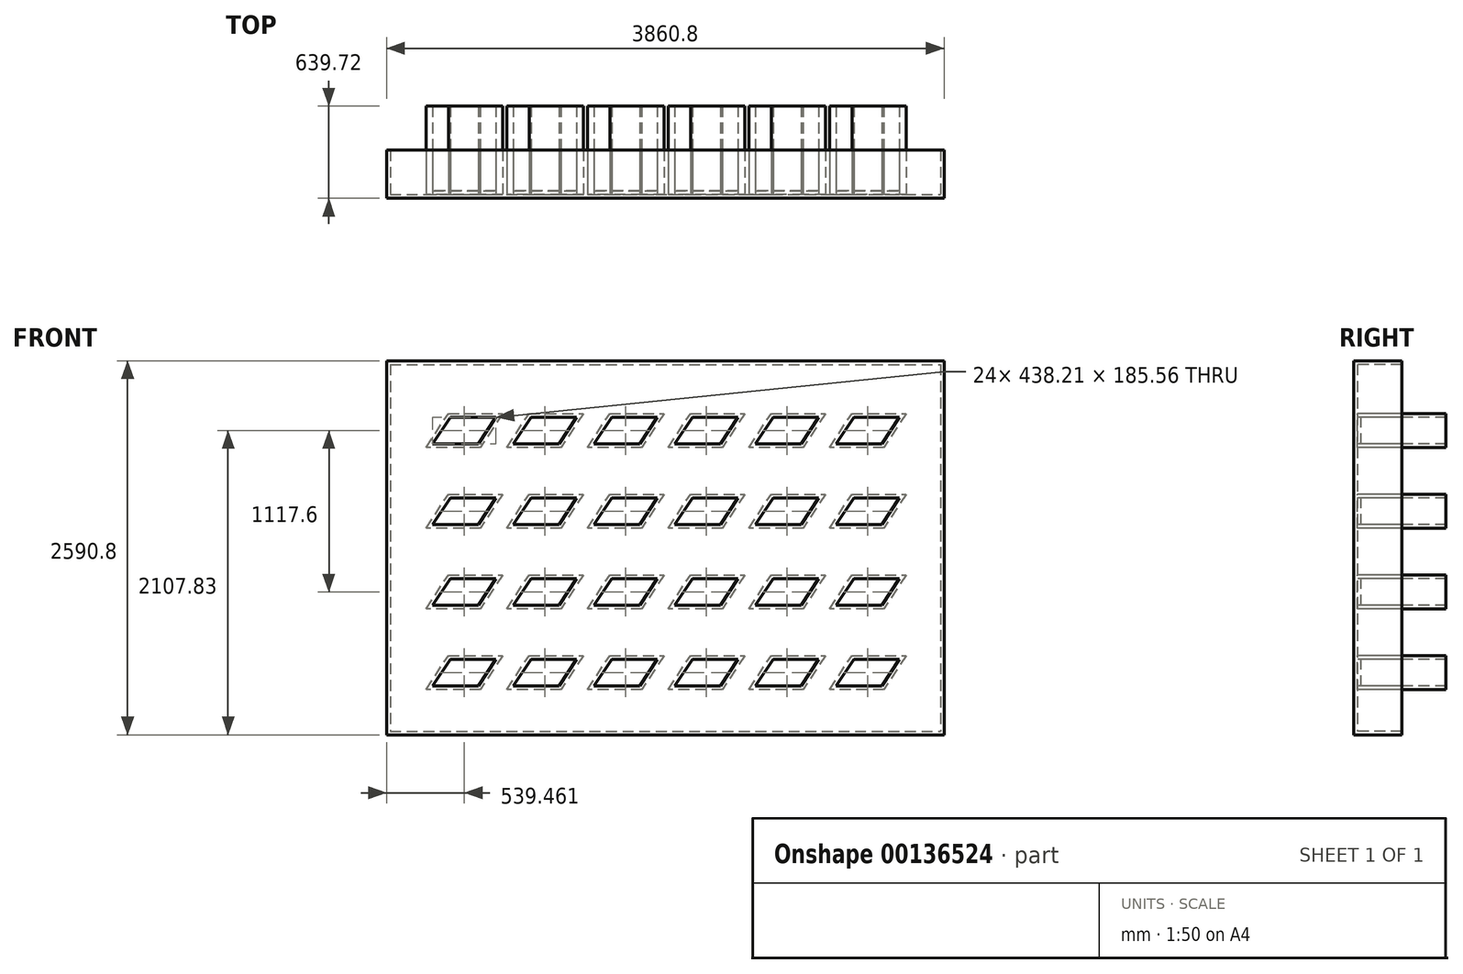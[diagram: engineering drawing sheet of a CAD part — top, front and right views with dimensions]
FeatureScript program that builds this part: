
annotation { "Feature Type Name" : "Feature", "Feature Type Description" : "" }
export const myFeature = defineFeature(function(context is Context, id is Id, definition is map)
    precondition{}
    {
        {
            var Q0;
            Q0=qCreatedBy(makeId("Front.planeOp"),FACE);
            var sketch = newSketch(context, id + "F0", { "sketchPlane" : qUnion([Q0])});
            skLineSegment(sketch, "E0.bottom", {"start": v(-2595.67, 2540) * mm, "end": v(1214.33, 2540) * mm});
            skLineSegment(sketch, "E0.top", {"start": v(-2595.67, 0) * mm, "end": v(1214.33, 0) * mm});
            skLineSegment(sketch, "E0.left", {"start": v(-2595.67, 2540) * mm, "end": v(-2595.67, 0) * mm});
            skLineSegment(sketch, "E0.right", {"start": v(1214.33, 2540) * mm, "end": v(1214.33, 0) * mm});
            skLineSegment(sketch, "E1", {"start": v(-2192.33, 2200.61) * mm, "end": v(-1815.39, 2200.61) * mm});
            skLineSegment(sketch, "E2", {"start": v(-1815.39, 2200.61) * mm, "end": v(-1970.89, 1964.26) * mm});
            skLineSegment(sketch, "E3", {"start": v(-1970.89, 1964.26) * mm, "end": v(-2347.83, 1964.26) * mm});
            skLineSegment(sketch, "E4", {"start": v(-2347.83, 1964.26) * mm, "end": v(-2192.33, 2200.61) * mm});
            skLineSegment(sketch, "E5.0.1.0", {"start": v(-2192.33, 1641.81) * mm, "end": v(-1815.39, 1641.81) * mm});
            skLineSegment(sketch, "E5.0.1.1", {"start": v(-2347.83, 1405.46) * mm, "end": v(-2192.33, 1641.81) * mm});
            skLineSegment(sketch, "E5.0.1.2", {"start": v(-1970.89, 1405.46) * mm, "end": v(-2347.83, 1405.46) * mm});
            skLineSegment(sketch, "E5.0.1.3", {"start": v(-1815.39, 1641.81) * mm, "end": v(-1970.89, 1405.46) * mm});
            skLineSegment(sketch, "E5.1.0.0", {"start": v(-1633.53, 2200.61) * mm, "end": v(-1256.59, 2200.61) * mm});
            skLineSegment(sketch, "E5.1.0.1", {"start": v(-1789.03, 1964.26) * mm, "end": v(-1633.53, 2200.61) * mm});
            skLineSegment(sketch, "E5.1.0.2", {"start": v(-1412.09, 1964.26) * mm, "end": v(-1789.03, 1964.26) * mm});
            skLineSegment(sketch, "E5.1.0.3", {"start": v(-1256.59, 2200.61) * mm, "end": v(-1412.09, 1964.26) * mm});
            skLineSegment(sketch, "E5.1.1.0", {"start": v(-1633.53, 1641.81) * mm, "end": v(-1256.59, 1641.81) * mm});
            skLineSegment(sketch, "E5.1.1.1", {"start": v(-1789.03, 1405.46) * mm, "end": v(-1633.53, 1641.81) * mm});
            skLineSegment(sketch, "E5.1.1.2", {"start": v(-1412.09, 1405.46) * mm, "end": v(-1789.03, 1405.46) * mm});
            skLineSegment(sketch, "E5.1.1.3", {"start": v(-1256.59, 1641.81) * mm, "end": v(-1412.09, 1405.46) * mm});
            skLineSegment(sketch, "E5.2.0.0", {"start": v(-1074.73, 2200.61) * mm, "end": v(-697.79, 2200.61) * mm});
            skLineSegment(sketch, "E5.2.0.1", {"start": v(-1230.23, 1964.26) * mm, "end": v(-1074.73, 2200.61) * mm});
            skLineSegment(sketch, "E5.2.0.2", {"start": v(-853.29, 1964.26) * mm, "end": v(-1230.23, 1964.26) * mm});
            skLineSegment(sketch, "E5.2.0.3", {"start": v(-697.79, 2200.61) * mm, "end": v(-853.29, 1964.26) * mm});
            skLineSegment(sketch, "E5.2.1.0", {"start": v(-1074.73, 1641.81) * mm, "end": v(-697.79, 1641.81) * mm});
            skLineSegment(sketch, "E5.2.1.1", {"start": v(-1230.23, 1405.46) * mm, "end": v(-1074.73, 1641.81) * mm});
            skLineSegment(sketch, "E5.2.1.2", {"start": v(-853.29, 1405.46) * mm, "end": v(-1230.23, 1405.46) * mm});
            skLineSegment(sketch, "E5.2.1.3", {"start": v(-697.79, 1641.81) * mm, "end": v(-853.29, 1405.46) * mm});
            skLineSegment(sketch, "E5.direction1", {"start": v(-2192.33, 2200.61) * mm, "end": v(-1633.53, 2200.61) * mm, "construction": true});
            skLineSegment(sketch, "E5.direction2", {"start": v(-2192.33, 2200.61) * mm, "end": v(-2192.33, 1641.81) * mm, "construction": true});
            skLineSegment(sketch, "E6.0.0.2", {"start": v(-2192.33, 1083.01) * mm, "end": v(-1815.39, 1083.01) * mm});
            skLineSegment(sketch, "E6.3.0.2", {"start": v(-2347.83, 846.66) * mm, "end": v(-2192.33, 1083.01) * mm});
            skLineSegment(sketch, "E6.6.0.2", {"start": v(-1970.89, 846.66) * mm, "end": v(-2347.83, 846.66) * mm});
            skLineSegment(sketch, "E6.9.0.2", {"start": v(-1815.39, 1083.01) * mm, "end": v(-1970.89, 846.66) * mm});
            skLineSegment(sketch, "E6.0.0.3", {"start": v(-2192.33, 524.21) * mm, "end": v(-1815.39, 524.21) * mm});
            skLineSegment(sketch, "E6.3.0.3", {"start": v(-2347.83, 287.86) * mm, "end": v(-2192.33, 524.21) * mm});
            skLineSegment(sketch, "E6.6.0.3", {"start": v(-1970.89, 287.86) * mm, "end": v(-2347.83, 287.86) * mm});
            skLineSegment(sketch, "E6.9.0.3", {"start": v(-1815.39, 524.21) * mm, "end": v(-1970.89, 287.86) * mm});
            skLineSegment(sketch, "E6.0.1.2", {"start": v(-1633.53, 1083.01) * mm, "end": v(-1256.59, 1083.01) * mm});
            skLineSegment(sketch, "E6.3.1.2", {"start": v(-1789.03, 846.66) * mm, "end": v(-1633.53, 1083.01) * mm});
            skLineSegment(sketch, "E6.6.1.2", {"start": v(-1412.09, 846.66) * mm, "end": v(-1789.03, 846.66) * mm});
            skLineSegment(sketch, "E6.9.1.2", {"start": v(-1256.59, 1083.01) * mm, "end": v(-1412.09, 846.66) * mm});
            skLineSegment(sketch, "E6.0.1.3", {"start": v(-1633.53, 524.21) * mm, "end": v(-1256.59, 524.21) * mm});
            skLineSegment(sketch, "E6.3.1.3", {"start": v(-1789.03, 287.86) * mm, "end": v(-1633.53, 524.21) * mm});
            skLineSegment(sketch, "E6.6.1.3", {"start": v(-1412.09, 287.86) * mm, "end": v(-1789.03, 287.86) * mm});
            skLineSegment(sketch, "E6.9.1.3", {"start": v(-1256.59, 524.21) * mm, "end": v(-1412.09, 287.86) * mm});
            skLineSegment(sketch, "E6.0.2.2", {"start": v(-1074.73, 1083.01) * mm, "end": v(-697.79, 1083.01) * mm});
            skLineSegment(sketch, "E6.3.2.2", {"start": v(-1230.23, 846.66) * mm, "end": v(-1074.73, 1083.01) * mm});
            skLineSegment(sketch, "E6.6.2.2", {"start": v(-853.29, 846.66) * mm, "end": v(-1230.23, 846.66) * mm});
            skLineSegment(sketch, "E6.9.2.2", {"start": v(-697.79, 1083.01) * mm, "end": v(-853.29, 846.66) * mm});
            skLineSegment(sketch, "E6.0.2.3", {"start": v(-1074.73, 524.21) * mm, "end": v(-697.79, 524.21) * mm});
            skLineSegment(sketch, "E6.3.2.3", {"start": v(-1230.23, 287.86) * mm, "end": v(-1074.73, 524.21) * mm});
            skLineSegment(sketch, "E6.6.2.3", {"start": v(-853.29, 287.86) * mm, "end": v(-1230.23, 287.86) * mm});
            skLineSegment(sketch, "E6.9.2.3", {"start": v(-697.79, 524.21) * mm, "end": v(-853.29, 287.86) * mm});
            skLineSegment(sketch, "E7.0.3.0", {"start": v(-515.93, 2200.61) * mm, "end": v(-138.99, 2200.61) * mm});
            skLineSegment(sketch, "E7.3.3.0", {"start": v(-671.43, 1964.26) * mm, "end": v(-515.93, 2200.61) * mm});
            skLineSegment(sketch, "E7.6.3.0", {"start": v(-294.49, 1964.26) * mm, "end": v(-671.43, 1964.26) * mm});
            skLineSegment(sketch, "E7.9.3.0", {"start": v(-138.99, 2200.61) * mm, "end": v(-294.49, 1964.26) * mm});
            skLineSegment(sketch, "E7.0.3.1", {"start": v(-515.93, 1641.81) * mm, "end": v(-138.99, 1641.81) * mm});
            skLineSegment(sketch, "E7.3.3.1", {"start": v(-671.43, 1405.46) * mm, "end": v(-515.93, 1641.81) * mm});
            skLineSegment(sketch, "E7.6.3.1", {"start": v(-294.49, 1405.46) * mm, "end": v(-671.43, 1405.46) * mm});
            skLineSegment(sketch, "E7.9.3.1", {"start": v(-138.99, 1641.81) * mm, "end": v(-294.49, 1405.46) * mm});
            skLineSegment(sketch, "E7.0.3.2", {"start": v(-515.93, 1083.01) * mm, "end": v(-138.99, 1083.01) * mm});
            skLineSegment(sketch, "E7.3.3.2", {"start": v(-671.43, 846.66) * mm, "end": v(-515.93, 1083.01) * mm});
            skLineSegment(sketch, "E7.6.3.2", {"start": v(-294.49, 846.66) * mm, "end": v(-671.43, 846.66) * mm});
            skLineSegment(sketch, "E7.9.3.2", {"start": v(-138.99, 1083.01) * mm, "end": v(-294.49, 846.66) * mm});
            skLineSegment(sketch, "E7.0.3.3", {"start": v(-515.93, 524.21) * mm, "end": v(-138.99, 524.21) * mm});
            skLineSegment(sketch, "E7.3.3.3", {"start": v(-671.43, 287.86) * mm, "end": v(-515.93, 524.21) * mm});
            skLineSegment(sketch, "E7.6.3.3", {"start": v(-294.49, 287.86) * mm, "end": v(-671.43, 287.86) * mm});
            skLineSegment(sketch, "E7.9.3.3", {"start": v(-138.99, 524.21) * mm, "end": v(-294.49, 287.86) * mm});
            skLineSegment(sketch, "E7.0.4.0", {"start": v(42.87, 2200.61) * mm, "end": v(419.81, 2200.61) * mm});
            skLineSegment(sketch, "E7.3.4.0", {"start": v(-112.63, 1964.26) * mm, "end": v(42.87, 2200.61) * mm});
            skLineSegment(sketch, "E7.6.4.0", {"start": v(264.31, 1964.26) * mm, "end": v(-112.63, 1964.26) * mm});
            skLineSegment(sketch, "E7.9.4.0", {"start": v(419.81, 2200.61) * mm, "end": v(264.31, 1964.26) * mm});
            skLineSegment(sketch, "E7.0.4.1", {"start": v(42.87, 1641.81) * mm, "end": v(419.81, 1641.81) * mm});
            skLineSegment(sketch, "E7.3.4.1", {"start": v(-112.63, 1405.46) * mm, "end": v(42.87, 1641.81) * mm});
            skLineSegment(sketch, "E7.6.4.1", {"start": v(264.31, 1405.46) * mm, "end": v(-112.63, 1405.46) * mm});
            skLineSegment(sketch, "E7.9.4.1", {"start": v(419.81, 1641.81) * mm, "end": v(264.31, 1405.46) * mm});
            skLineSegment(sketch, "E7.0.4.2", {"start": v(42.87, 1083.01) * mm, "end": v(419.81, 1083.01) * mm});
            skLineSegment(sketch, "E7.3.4.2", {"start": v(-112.63, 846.66) * mm, "end": v(42.87, 1083.01) * mm});
            skLineSegment(sketch, "E7.6.4.2", {"start": v(264.31, 846.66) * mm, "end": v(-112.63, 846.66) * mm});
            skLineSegment(sketch, "E7.9.4.2", {"start": v(419.81, 1083.01) * mm, "end": v(264.31, 846.66) * mm});
            skLineSegment(sketch, "E7.0.4.3", {"start": v(42.87, 524.21) * mm, "end": v(419.81, 524.21) * mm});
            skLineSegment(sketch, "E7.3.4.3", {"start": v(-112.63, 287.86) * mm, "end": v(42.87, 524.21) * mm});
            skLineSegment(sketch, "E7.6.4.3", {"start": v(264.31, 287.86) * mm, "end": v(-112.63, 287.86) * mm});
            skLineSegment(sketch, "E7.9.4.3", {"start": v(419.81, 524.21) * mm, "end": v(264.31, 287.86) * mm});
            skLineSegment(sketch, "E7.0.5.0", {"start": v(601.67, 2200.61) * mm, "end": v(978.61, 2200.61) * mm});
            skLineSegment(sketch, "E7.3.5.0", {"start": v(446.17, 1964.26) * mm, "end": v(601.67, 2200.61) * mm});
            skLineSegment(sketch, "E7.6.5.0", {"start": v(823.11, 1964.26) * mm, "end": v(446.17, 1964.26) * mm});
            skLineSegment(sketch, "E7.9.5.0", {"start": v(978.61, 2200.61) * mm, "end": v(823.11, 1964.26) * mm});
            skLineSegment(sketch, "E7.0.5.1", {"start": v(601.67, 1641.81) * mm, "end": v(978.61, 1641.81) * mm});
            skLineSegment(sketch, "E7.3.5.1", {"start": v(446.17, 1405.46) * mm, "end": v(601.67, 1641.81) * mm});
            skLineSegment(sketch, "E7.6.5.1", {"start": v(823.11, 1405.46) * mm, "end": v(446.17, 1405.46) * mm});
            skLineSegment(sketch, "E7.9.5.1", {"start": v(978.61, 1641.81) * mm, "end": v(823.11, 1405.46) * mm});
            skLineSegment(sketch, "E7.0.5.2", {"start": v(601.67, 1083.01) * mm, "end": v(978.61, 1083.01) * mm});
            skLineSegment(sketch, "E7.3.5.2", {"start": v(446.17, 846.66) * mm, "end": v(601.67, 1083.01) * mm});
            skLineSegment(sketch, "E7.6.5.2", {"start": v(823.11, 846.66) * mm, "end": v(446.17, 846.66) * mm});
            skLineSegment(sketch, "E7.9.5.2", {"start": v(978.61, 1083.01) * mm, "end": v(823.11, 846.66) * mm});
            skLineSegment(sketch, "E7.0.5.3", {"start": v(601.67, 524.21) * mm, "end": v(978.61, 524.21) * mm});
            skLineSegment(sketch, "E7.3.5.3", {"start": v(446.17, 287.86) * mm, "end": v(601.67, 524.21) * mm});
            skLineSegment(sketch, "E7.6.5.3", {"start": v(823.11, 287.86) * mm, "end": v(446.17, 287.86) * mm});
            skLineSegment(sketch, "E7.9.5.3", {"start": v(978.61, 524.21) * mm, "end": v(823.11, 287.86) * mm});
            skSolve(sketch);
        }
        {
            var Q0;
            Q0=makeQuery(id+"F0.imprint","IMPRINT",FACE,{"disambiguationData":[TD([[makeQuery(id+"F0.imprint","IMPRINT",EDGE,{"derivedFrom":sQuery(id+"F0.wireOp",EDGE,"E7.0.5.2")}),-1.0]])]});
            var Q1;
            Q1=makeQuery(id+"F0.imprint","IMPRINT",FACE,{"disambiguationData":[TD([[makeQuery(id+"F0.imprint","IMPRINT",EDGE,{"derivedFrom":sQuery(id+"F0.wireOp",EDGE,"E7.0.5.3")}),-1.0]])]});
            var Q2;
            Q2=makeQuery(id+"F0.imprint","IMPRINT",FACE,{"disambiguationData":[TD([[makeQuery(id+"F0.imprint","IMPRINT",EDGE,{"derivedFrom":sQuery(id+"F0.wireOp",EDGE,"E7.0.5.1")}),-1.0]])]});
            var Q3;
            Q3=makeQuery(id+"F0.imprint","IMPRINT",FACE,{"disambiguationData":[TD([[makeQuery(id+"F0.imprint","IMPRINT",EDGE,{"derivedFrom":sQuery(id+"F0.wireOp",EDGE,"E7.0.5.0")}),-1.0]])]});
            var Q4;
            Q4=makeQuery(id+"F0.imprint","IMPRINT",FACE,{"disambiguationData":[TD([[makeQuery(id+"F0.imprint","IMPRINT",EDGE,{"derivedFrom":sQuery(id+"F0.wireOp",EDGE,"E7.0.4.3")}),-1.0]])]});
            var Q5;
            Q5=makeQuery(id+"F0.imprint","IMPRINT",FACE,{"disambiguationData":[TD([[makeQuery(id+"F0.imprint","IMPRINT",EDGE,{"derivedFrom":sQuery(id+"F0.wireOp",EDGE,"E7.0.4.2")}),-1.0]])]});
            var Q6;
            Q6=makeQuery(id+"F0.imprint","IMPRINT",FACE,{"disambiguationData":[TD([[makeQuery(id+"F0.imprint","IMPRINT",EDGE,{"derivedFrom":sQuery(id+"F0.wireOp",EDGE,"E7.0.4.1")}),-1.0]])]});
            var Q7;
            Q7=makeQuery(id+"F0.imprint","IMPRINT",FACE,{"disambiguationData":[TD([[makeQuery(id+"F0.imprint","IMPRINT",EDGE,{"derivedFrom":sQuery(id+"F0.wireOp",EDGE,"E7.0.4.0")}),-1.0]])]});
            var Q8;
            Q8=makeQuery(id+"F0.imprint","IMPRINT",FACE,{"disambiguationData":[TD([[makeQuery(id+"F0.imprint","IMPRINT",EDGE,{"derivedFrom":sQuery(id+"F0.wireOp",EDGE,"E7.0.3.3")}),-1.0]])]});
            var Q9;
            Q9=makeQuery(id+"F0.imprint","IMPRINT",FACE,{"disambiguationData":[TD([[makeQuery(id+"F0.imprint","IMPRINT",EDGE,{"derivedFrom":sQuery(id+"F0.wireOp",EDGE,"E7.0.3.2")}),-1.0]])]});
            var Q10;
            Q10=makeQuery(id+"F0.imprint","IMPRINT",FACE,{"disambiguationData":[TD([[makeQuery(id+"F0.imprint","IMPRINT",EDGE,{"derivedFrom":sQuery(id+"F0.wireOp",EDGE,"E7.0.3.1")}),-1.0]])]});
            var Q11;
            Q11=makeQuery(id+"F0.imprint","IMPRINT",FACE,{"disambiguationData":[TD([[makeQuery(id+"F0.imprint","IMPRINT",EDGE,{"derivedFrom":sQuery(id+"F0.wireOp",EDGE,"E7.0.3.0")}),-1.0]])]});
            var Q12;
            Q12=makeQuery(id+"F0.imprint","IMPRINT",FACE,{"disambiguationData":[TD([[makeQuery(id+"F0.imprint","IMPRINT",EDGE,{"derivedFrom":sQuery(id+"F0.wireOp",EDGE,"E6.0.2.3")}),-1.0]])]});
            var Q13;
            Q13=makeQuery(id+"F0.imprint","IMPRINT",FACE,{"disambiguationData":[TD([[makeQuery(id+"F0.imprint","IMPRINT",EDGE,{"derivedFrom":sQuery(id+"F0.wireOp",EDGE,"E6.0.2.2")}),-1.0]])]});
            var Q14;
            Q14=makeQuery(id+"F0.imprint","IMPRINT",FACE,{"disambiguationData":[TD([[makeQuery(id+"F0.imprint","IMPRINT",EDGE,{"derivedFrom":sQuery(id+"F0.wireOp",EDGE,"E5.2.1.0")}),-1.0]])]});
            var Q15;
            Q15=makeQuery(id+"F0.imprint","IMPRINT",FACE,{"disambiguationData":[TD([[makeQuery(id+"F0.imprint","IMPRINT",EDGE,{"derivedFrom":sQuery(id+"F0.wireOp",EDGE,"E5.2.0.0")}),-1.0]])]});
            var Q16;
            Q16=makeQuery(id+"F0.imprint","IMPRINT",FACE,{"disambiguationData":[TD([[makeQuery(id+"F0.imprint","IMPRINT",EDGE,{"derivedFrom":sQuery(id+"F0.wireOp",EDGE,"E6.0.1.3")}),-1.0]])]});
            var Q17;
            Q17=makeQuery(id+"F0.imprint","IMPRINT",FACE,{"disambiguationData":[TD([[makeQuery(id+"F0.imprint","IMPRINT",EDGE,{"derivedFrom":sQuery(id+"F0.wireOp",EDGE,"E6.0.1.2")}),-1.0]])]});
            var Q18;
            Q18=makeQuery(id+"F0.imprint","IMPRINT",FACE,{"disambiguationData":[TD([[makeQuery(id+"F0.imprint","IMPRINT",EDGE,{"derivedFrom":sQuery(id+"F0.wireOp",EDGE,"E5.1.1.0")}),-1.0]])]});
            var Q19;
            Q19=makeQuery(id+"F0.imprint","IMPRINT",FACE,{"disambiguationData":[TD([[makeQuery(id+"F0.imprint","IMPRINT",EDGE,{"derivedFrom":sQuery(id+"F0.wireOp",EDGE,"E5.1.0.0")}),-1.0]])]});
            var Q20;
            Q20=makeQuery(id+"F0.imprint","IMPRINT",FACE,{"disambiguationData":[TD([[makeQuery(id+"F0.imprint","IMPRINT",EDGE,{"derivedFrom":sQuery(id+"F0.wireOp",EDGE,"E6.0.0.3")}),-1.0]])]});
            var Q21;
            Q21=makeQuery(id+"F0.imprint","IMPRINT",FACE,{"disambiguationData":[TD([[makeQuery(id+"F0.imprint","IMPRINT",EDGE,{"derivedFrom":sQuery(id+"F0.wireOp",EDGE,"E6.0.0.2")}),-1.0]])]});
            var Q22;
            Q22=makeQuery(id+"F0.imprint","IMPRINT",FACE,{"disambiguationData":[TD([[makeQuery(id+"F0.imprint","IMPRINT",EDGE,{"derivedFrom":sQuery(id+"F0.wireOp",EDGE,"E5.0.1.0")}),-1.0]])]});
            var Q23;
            Q23=makeQuery(id+"F0.imprint","IMPRINT",FACE,{"disambiguationData":[TD([[makeQuery(id+"F0.imprint","IMPRINT",EDGE,{"derivedFrom":sQuery(id+"F0.wireOp",EDGE,"E1")}),-1.0]])]});
            extrude(context, id + "F1", {"entities" : qUnion([Q0, Q1, Q2, Q3, Q4, Q5, Q6, Q7, Q8, Q9, Q10, Q11, Q12, Q13, Q14, Q15, Q16, Q17, Q18, Q19, Q20, Q21, Q22, Q23]), "oppositeDirection" : true, "depth" : 614.32 * mm});
        }
        {
            var Q0;
            Q0=makeQuery(id+"F1.opExtrude","CAP_FACE",FACE,{"disambiguationData":[OSD([sQuery(id+"F0.wireOp",EDGE,"E7.0.5.0"),sQuery(id+"F0.wireOp",EDGE,"E7.3.5.0"),sQuery(id+"F0.wireOp",EDGE,"E7.6.5.0"),sQuery(id+"F0.wireOp",EDGE,"E7.9.5.0")])],"isStart":false});
            var Q1;
            Q1=makeQuery(id+"F1.opExtrude","CAP_FACE",FACE,{"disambiguationData":[OSD([sQuery(id+"F0.wireOp",EDGE,"E7.0.5.1"),sQuery(id+"F0.wireOp",EDGE,"E7.3.5.1"),sQuery(id+"F0.wireOp",EDGE,"E7.6.5.1"),sQuery(id+"F0.wireOp",EDGE,"E7.9.5.1")])],"isStart":false});
            var Q2;
            Q2=makeQuery(id+"F1.opExtrude","CAP_FACE",FACE,{"disambiguationData":[OSD([sQuery(id+"F0.wireOp",EDGE,"E7.0.4.1"),sQuery(id+"F0.wireOp",EDGE,"E7.3.4.1"),sQuery(id+"F0.wireOp",EDGE,"E7.6.4.1"),sQuery(id+"F0.wireOp",EDGE,"E7.9.4.1")])],"isStart":false});
            var Q3;
            Q3=makeQuery(id+"F1.opExtrude","CAP_FACE",FACE,{"disambiguationData":[OSD([sQuery(id+"F0.wireOp",EDGE,"E7.0.4.0"),sQuery(id+"F0.wireOp",EDGE,"E7.3.4.0"),sQuery(id+"F0.wireOp",EDGE,"E7.6.4.0"),sQuery(id+"F0.wireOp",EDGE,"E7.9.4.0")])],"isStart":false});
            var Q4;
            Q4=makeQuery(id+"F1.opExtrude","CAP_FACE",FACE,{"disambiguationData":[OSD([sQuery(id+"F0.wireOp",EDGE,"E7.0.4.2"),sQuery(id+"F0.wireOp",EDGE,"E7.3.4.2"),sQuery(id+"F0.wireOp",EDGE,"E7.6.4.2"),sQuery(id+"F0.wireOp",EDGE,"E7.9.4.2")])],"isStart":false});
            var Q5;
            Q5=makeQuery(id+"F1.opExtrude","CAP_FACE",FACE,{"disambiguationData":[OSD([sQuery(id+"F0.wireOp",EDGE,"E7.0.3.2"),sQuery(id+"F0.wireOp",EDGE,"E7.3.3.2"),sQuery(id+"F0.wireOp",EDGE,"E7.6.3.2"),sQuery(id+"F0.wireOp",EDGE,"E7.9.3.2")])],"isStart":false});
            var Q6;
            Q6=makeQuery(id+"F1.opExtrude","CAP_FACE",FACE,{"disambiguationData":[OSD([sQuery(id+"F0.wireOp",EDGE,"E7.0.5.2"),sQuery(id+"F0.wireOp",EDGE,"E7.3.5.2"),sQuery(id+"F0.wireOp",EDGE,"E7.6.5.2"),sQuery(id+"F0.wireOp",EDGE,"E7.9.5.2")])],"isStart":false});
            var Q7;
            Q7=makeQuery(id+"F1.opExtrude","CAP_FACE",FACE,{"disambiguationData":[OSD([sQuery(id+"F0.wireOp",EDGE,"E7.0.5.3"),sQuery(id+"F0.wireOp",EDGE,"E7.3.5.3"),sQuery(id+"F0.wireOp",EDGE,"E7.6.5.3"),sQuery(id+"F0.wireOp",EDGE,"E7.9.5.3")])],"isStart":false});
            var Q8;
            Q8=makeQuery(id+"F1.opExtrude","CAP_FACE",FACE,{"disambiguationData":[OSD([sQuery(id+"F0.wireOp",EDGE,"E7.0.3.3"),sQuery(id+"F0.wireOp",EDGE,"E7.3.3.3"),sQuery(id+"F0.wireOp",EDGE,"E7.6.3.3"),sQuery(id+"F0.wireOp",EDGE,"E7.9.3.3")])],"isStart":false});
            var Q9;
            Q9=makeQuery(id+"F1.opExtrude","CAP_FACE",FACE,{"disambiguationData":[OSD([sQuery(id+"F0.wireOp",EDGE,"E7.0.3.1"),sQuery(id+"F0.wireOp",EDGE,"E7.3.3.1"),sQuery(id+"F0.wireOp",EDGE,"E7.6.3.1"),sQuery(id+"F0.wireOp",EDGE,"E7.9.3.1")])],"isStart":false});
            var Q10;
            Q10=makeQuery(id+"F1.opExtrude","CAP_FACE",FACE,{"disambiguationData":[OSD([sQuery(id+"F0.wireOp",EDGE,"E7.0.3.0"),sQuery(id+"F0.wireOp",EDGE,"E7.3.3.0"),sQuery(id+"F0.wireOp",EDGE,"E7.6.3.0"),sQuery(id+"F0.wireOp",EDGE,"E7.9.3.0")])],"isStart":false});
            var Q11;
            Q11=makeQuery(id+"F1.opExtrude","CAP_FACE",FACE,{"disambiguationData":[OSD([sQuery(id+"F0.wireOp",EDGE,"E6.0.2.2"),sQuery(id+"F0.wireOp",EDGE,"E6.3.2.2"),sQuery(id+"F0.wireOp",EDGE,"E6.6.2.2"),sQuery(id+"F0.wireOp",EDGE,"E6.9.2.2")])],"isStart":false});
            var Q12;
            Q12=makeQuery(id+"F1.opExtrude","CAP_FACE",FACE,{"disambiguationData":[OSD([sQuery(id+"F0.wireOp",EDGE,"E5.2.1.0"),sQuery(id+"F0.wireOp",EDGE,"E5.2.1.1"),sQuery(id+"F0.wireOp",EDGE,"E5.2.1.2"),sQuery(id+"F0.wireOp",EDGE,"E5.2.1.3")])],"isStart":false});
            var Q13;
            Q13=makeQuery(id+"F1.opExtrude","CAP_FACE",FACE,{"disambiguationData":[OSD([sQuery(id+"F0.wireOp",EDGE,"E5.2.0.0"),sQuery(id+"F0.wireOp",EDGE,"E5.2.0.1"),sQuery(id+"F0.wireOp",EDGE,"E5.2.0.2"),sQuery(id+"F0.wireOp",EDGE,"E5.2.0.3")])],"isStart":false});
            var Q14;
            Q14=makeQuery(id+"F1.opExtrude","CAP_FACE",FACE,{"disambiguationData":[OSD([sQuery(id+"F0.wireOp",EDGE,"E6.0.1.3"),sQuery(id+"F0.wireOp",EDGE,"E6.3.1.3"),sQuery(id+"F0.wireOp",EDGE,"E6.6.1.3"),sQuery(id+"F0.wireOp",EDGE,"E6.9.1.3")])],"isStart":false});
            var Q15;
            Q15=makeQuery(id+"F1.opExtrude","CAP_FACE",FACE,{"disambiguationData":[OSD([sQuery(id+"F0.wireOp",EDGE,"E6.0.1.2"),sQuery(id+"F0.wireOp",EDGE,"E6.3.1.2"),sQuery(id+"F0.wireOp",EDGE,"E6.6.1.2"),sQuery(id+"F0.wireOp",EDGE,"E6.9.1.2")])],"isStart":false});
            var Q16;
            Q16=makeQuery(id+"F1.opExtrude","CAP_FACE",FACE,{"disambiguationData":[OSD([sQuery(id+"F0.wireOp",EDGE,"E5.1.1.0"),sQuery(id+"F0.wireOp",EDGE,"E5.1.1.1"),sQuery(id+"F0.wireOp",EDGE,"E5.1.1.2"),sQuery(id+"F0.wireOp",EDGE,"E5.1.1.3")])],"isStart":false});
            var Q17;
            Q17=makeQuery(id+"F1.opExtrude","CAP_FACE",FACE,{"disambiguationData":[OSD([sQuery(id+"F0.wireOp",EDGE,"E5.1.0.0"),sQuery(id+"F0.wireOp",EDGE,"E5.1.0.1"),sQuery(id+"F0.wireOp",EDGE,"E5.1.0.2"),sQuery(id+"F0.wireOp",EDGE,"E5.1.0.3")])],"isStart":false});
            var Q18;
            Q18=makeQuery(id+"F1.opExtrude","CAP_FACE",FACE,{"disambiguationData":[OSD([sQuery(id+"F0.wireOp",EDGE,"E1"),sQuery(id+"F0.wireOp",EDGE,"E2"),sQuery(id+"F0.wireOp",EDGE,"E3"),sQuery(id+"F0.wireOp",EDGE,"E4")])],"isStart":false});
            var Q19;
            Q19=makeQuery(id+"F1.opExtrude","CAP_FACE",FACE,{"disambiguationData":[OSD([sQuery(id+"F0.wireOp",EDGE,"E5.0.1.0"),sQuery(id+"F0.wireOp",EDGE,"E5.0.1.1"),sQuery(id+"F0.wireOp",EDGE,"E5.0.1.2"),sQuery(id+"F0.wireOp",EDGE,"E5.0.1.3")])],"isStart":false});
            var Q20;
            Q20=makeQuery(id+"F1.opExtrude","CAP_FACE",FACE,{"disambiguationData":[OSD([sQuery(id+"F0.wireOp",EDGE,"E6.0.0.2"),sQuery(id+"F0.wireOp",EDGE,"E6.3.0.2"),sQuery(id+"F0.wireOp",EDGE,"E6.6.0.2"),sQuery(id+"F0.wireOp",EDGE,"E6.9.0.2")])],"isStart":false});
            var Q21;
            Q21=makeQuery(id+"F1.opExtrude","CAP_FACE",FACE,{"disambiguationData":[OSD([sQuery(id+"F0.wireOp",EDGE,"E6.0.0.3"),sQuery(id+"F0.wireOp",EDGE,"E6.3.0.3"),sQuery(id+"F0.wireOp",EDGE,"E6.6.0.3"),sQuery(id+"F0.wireOp",EDGE,"E6.9.0.3")])],"isStart":false});
            var Q22;
            Q22=makeQuery(id+"F1.opExtrude","CAP_FACE",FACE,{"disambiguationData":[OSD([sQuery(id+"F0.wireOp",EDGE,"E6.0.2.3"),sQuery(id+"F0.wireOp",EDGE,"E6.3.2.3"),sQuery(id+"F0.wireOp",EDGE,"E6.6.2.3"),sQuery(id+"F0.wireOp",EDGE,"E6.9.2.3")])],"isStart":false});
            var Q23;
            Q23=makeQuery(id+"F1.opExtrude","CAP_FACE",FACE,{"disambiguationData":[OSD([sQuery(id+"F0.wireOp",EDGE,"E7.0.4.3"),sQuery(id+"F0.wireOp",EDGE,"E7.3.4.3"),sQuery(id+"F0.wireOp",EDGE,"E7.6.4.3"),sQuery(id+"F0.wireOp",EDGE,"E7.9.4.3")])],"isStart":false});
            shell(context, id + "F2", {"entities" : qUnion([Q0, Q1, Q2, Q3, Q4, Q5, Q6, Q7, Q8, Q9, Q10, Q11, Q12, Q13, Q14, Q15, Q16, Q17, Q18, Q19, Q20, Q21, Q22, Q23]), "thickness" : 25.4 * mm});
        }
        {
            var Q0;
            Q0=makeQuery(id+"F0.imprint","IMPRINT",FACE,{"disambiguationData":[TD([[makeQuery(id+"F0.imprint","IMPRINT",EDGE,{"derivedFrom":sQuery(id+"F0.wireOp",EDGE,"E0.bottom")}),-1.0]])]});
            extrude(context, id + "F3", {"entities" : qUnion([Q0]), "oppositeDirection" : true, "depth" : 308.55 * mm});
        }
        {
            var Q0;
            Q0=makeQuery(id+"F3.opExtrude","CAP_FACE",FACE,{"disambiguationData":[OSD([sQuery(id+"F0.wireOp",EDGE,"E0.bottom"),sQuery(id+"F0.wireOp",EDGE,"E0.top"),sQuery(id+"F0.wireOp",EDGE,"E0.left"),sQuery(id+"F0.wireOp",EDGE,"E0.right"),sQuery(id+"F0.wireOp",EDGE,"E1"),sQuery(id+"F0.wireOp",EDGE,"E2"),sQuery(id+"F0.wireOp",EDGE,"E3"),sQuery(id+"F0.wireOp",EDGE,"E4"),sQuery(id+"F0.wireOp",EDGE,"E5.0.1.0"),sQuery(id+"F0.wireOp",EDGE,"E5.0.1.1"),sQuery(id+"F0.wireOp",EDGE,"E5.0.1.2"),sQuery(id+"F0.wireOp",EDGE,"E5.0.1.3"),sQuery(id+"F0.wireOp",EDGE,"E5.1.0.0"),sQuery(id+"F0.wireOp",EDGE,"E5.1.0.1"),sQuery(id+"F0.wireOp",EDGE,"E5.1.0.2"),sQuery(id+"F0.wireOp",EDGE,"E5.1.0.3"),sQuery(id+"F0.wireOp",EDGE,"E5.1.1.0"),sQuery(id+"F0.wireOp",EDGE,"E5.1.1.1"),sQuery(id+"F0.wireOp",EDGE,"E5.1.1.2"),sQuery(id+"F0.wireOp",EDGE,"E5.1.1.3"),sQuery(id+"F0.wireOp",EDGE,"E5.2.0.0"),sQuery(id+"F0.wireOp",EDGE,"E5.2.0.1"),sQuery(id+"F0.wireOp",EDGE,"E5.2.0.2"),sQuery(id+"F0.wireOp",EDGE,"E5.2.0.3"),sQuery(id+"F0.wireOp",EDGE,"E5.2.1.0"),sQuery(id+"F0.wireOp",EDGE,"E5.2.1.1"),sQuery(id+"F0.wireOp",EDGE,"E5.2.1.2"),sQuery(id+"F0.wireOp",EDGE,"E5.2.1.3"),sQuery(id+"F0.wireOp",EDGE,"E6.0.0.2"),sQuery(id+"F0.wireOp",EDGE,"E6.3.0.2"),sQuery(id+"F0.wireOp",EDGE,"E6.6.0.2"),sQuery(id+"F0.wireOp",EDGE,"E6.9.0.2"),sQuery(id+"F0.wireOp",EDGE,"E6.0.0.3"),sQuery(id+"F0.wireOp",EDGE,"E6.3.0.3"),sQuery(id+"F0.wireOp",EDGE,"E6.6.0.3"),sQuery(id+"F0.wireOp",EDGE,"E6.9.0.3"),sQuery(id+"F0.wireOp",EDGE,"E6.0.1.2"),sQuery(id+"F0.wireOp",EDGE,"E6.3.1.2"),sQuery(id+"F0.wireOp",EDGE,"E6.6.1.2"),sQuery(id+"F0.wireOp",EDGE,"E6.9.1.2"),sQuery(id+"F0.wireOp",EDGE,"E6.0.1.3"),sQuery(id+"F0.wireOp",EDGE,"E6.3.1.3"),sQuery(id+"F0.wireOp",EDGE,"E6.6.1.3"),sQuery(id+"F0.wireOp",EDGE,"E6.9.1.3"),sQuery(id+"F0.wireOp",EDGE,"E6.0.2.2"),sQuery(id+"F0.wireOp",EDGE,"E6.3.2.2"),sQuery(id+"F0.wireOp",EDGE,"E6.6.2.2"),sQuery(id+"F0.wireOp",EDGE,"E6.9.2.2"),sQuery(id+"F0.wireOp",EDGE,"E6.0.2.3"),sQuery(id+"F0.wireOp",EDGE,"E6.3.2.3"),sQuery(id+"F0.wireOp",EDGE,"E6.6.2.3"),sQuery(id+"F0.wireOp",EDGE,"E6.9.2.3"),sQuery(id+"F0.wireOp",EDGE,"E7.0.3.0"),sQuery(id+"F0.wireOp",EDGE,"E7.3.3.0"),sQuery(id+"F0.wireOp",EDGE,"E7.6.3.0"),sQuery(id+"F0.wireOp",EDGE,"E7.9.3.0"),sQuery(id+"F0.wireOp",EDGE,"E7.0.3.1"),sQuery(id+"F0.wireOp",EDGE,"E7.3.3.1"),sQuery(id+"F0.wireOp",EDGE,"E7.6.3.1"),sQuery(id+"F0.wireOp",EDGE,"E7.9.3.1"),sQuery(id+"F0.wireOp",EDGE,"E7.0.3.2"),sQuery(id+"F0.wireOp",EDGE,"E7.3.3.2"),sQuery(id+"F0.wireOp",EDGE,"E7.6.3.2"),sQuery(id+"F0.wireOp",EDGE,"E7.9.3.2"),sQuery(id+"F0.wireOp",EDGE,"E7.0.3.3"),sQuery(id+"F0.wireOp",EDGE,"E7.3.3.3"),sQuery(id+"F0.wireOp",EDGE,"E7.6.3.3"),sQuery(id+"F0.wireOp",EDGE,"E7.9.3.3"),sQuery(id+"F0.wireOp",EDGE,"E7.0.4.0"),sQuery(id+"F0.wireOp",EDGE,"E7.3.4.0"),sQuery(id+"F0.wireOp",EDGE,"E7.6.4.0"),sQuery(id+"F0.wireOp",EDGE,"E7.9.4.0"),sQuery(id+"F0.wireOp",EDGE,"E7.0.4.1"),sQuery(id+"F0.wireOp",EDGE,"E7.3.4.1"),sQuery(id+"F0.wireOp",EDGE,"E7.6.4.1"),sQuery(id+"F0.wireOp",EDGE,"E7.9.4.1"),sQuery(id+"F0.wireOp",EDGE,"E7.0.4.2"),sQuery(id+"F0.wireOp",EDGE,"E7.3.4.2"),sQuery(id+"F0.wireOp",EDGE,"E7.6.4.2"),sQuery(id+"F0.wireOp",EDGE,"E7.9.4.2"),sQuery(id+"F0.wireOp",EDGE,"E7.0.4.3"),sQuery(id+"F0.wireOp",EDGE,"E7.3.4.3"),sQuery(id+"F0.wireOp",EDGE,"E7.6.4.3"),sQuery(id+"F0.wireOp",EDGE,"E7.9.4.3"),sQuery(id+"F0.wireOp",EDGE,"E7.0.5.0"),sQuery(id+"F0.wireOp",EDGE,"E7.3.5.0"),sQuery(id+"F0.wireOp",EDGE,"E7.6.5.0"),sQuery(id+"F0.wireOp",EDGE,"E7.9.5.0"),sQuery(id+"F0.wireOp",EDGE,"E7.0.5.1"),sQuery(id+"F0.wireOp",EDGE,"E7.3.5.1"),sQuery(id+"F0.wireOp",EDGE,"E7.6.5.1"),sQuery(id+"F0.wireOp",EDGE,"E7.9.5.1"),sQuery(id+"F0.wireOp",EDGE,"E7.0.5.2"),sQuery(id+"F0.wireOp",EDGE,"E7.3.5.2"),sQuery(id+"F0.wireOp",EDGE,"E7.6.5.2"),sQuery(id+"F0.wireOp",EDGE,"E7.9.5.2"),sQuery(id+"F0.wireOp",EDGE,"E7.0.5.3"),sQuery(id+"F0.wireOp",EDGE,"E7.3.5.3"),sQuery(id+"F0.wireOp",EDGE,"E7.6.5.3"),sQuery(id+"F0.wireOp",EDGE,"E7.9.5.3")])],"isStart":false});
            shell(context, id + "F4", {"entities" : qUnion([Q0]), "thickness" : 25.4 * mm, "oppositeDirection" : true});
        }
    });
